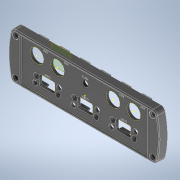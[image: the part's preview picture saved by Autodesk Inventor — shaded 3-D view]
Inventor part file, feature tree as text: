
AUTODESK INVENTOR PART (.ipt)
format: ipt  version: 2021 (Build 250183000, 183)  size: 1,043,968 bytes
history: native  units: mm
features: sketch x8, extrude x7, chamfer x5, plane x3, fillet x2, mirror x1, hole x1, other x1
ambient origin geometry x8: Origin, YZ Plane, XZ Plane, XY Plane, X Axis, Y Axis, Z Axis, Center Point
bodies: Solid1 (feature_tree)
feature tree (28):
  extrude  "Extrusion1"  TaperAngle=0.0deg  [1 undecoded]
  fillet  "Fillet1"  Radius=6.9mm
  plane  "Work Plane1"
  extrude  "Extrusion4"  [1 undecoded]
  chamfer  "Chamfer2"  [1 undecoded]
  mirror  "Mirror1"
  plane  "Work Plane2"
  extrude  "Extrusion7"  Depth=0.2mm TaperAngle=45.0deg
  chamfer  "Chamfer3"  Distance=5.225mm
  hole  "Hole1"  [1 undecoded]
  plane  "Work Plane3"
  extrude  "Extrusion11"  Depth=0.2mm
  extrude  "Extrusion12"  Depth=0.2mm
  fillet  "Fillet4"  Radius=7.0mm
  chamfer  "Chamfer4"  Distance=10.0mm
  chamfer  "Chamfer5"  Distance=0.5mm Angle=45.0deg
  extrude  "Extrusion13"  Depth=0.2mm
  sketch  "Sketch20"  dims[d44=0.0mm]
  extrude  "Extrusion14"  Depth=0.2mm
  chamfer  "Chamfer6"  Distance=12.0mm
  sketch  "Sketch1"  dims[d3=9.0mm d15=0.0mm d16=0.0mm d21=6.9mm]
  sketch  "Sketch5"  dims[d23=1.35mm d26=-1.5mm]
  sketch  "Sketch15"  dims[d40=15.4mm]
  sketch  "Sketch17"  dims[d41=11.5mm]
  sketch  "Sketch18"  dims[d42=54.0mm]
  sketch  "Sketch19"  dims[d43=15.4mm]
  sketch  "Sketch22"  dims[d45=31.0mm d46=0.0mm d47=0.0mm d48=0.2mm d49=2.0mm d50=45.0deg d65=4.85mm d66=4.85mm d67=27.0mm d68=9.0mm d69=3.3mm d70=3.3mm d71=24.0mm d72=16.55mm d73=11.55mm d74=6.35mm d75=1.85mm d76=5.225mm d77=6.9mm d78=10.075mm d79=10.075mm d80=42.584mm d82=7.0mm d83=10.0mm d84=0.0mm d85=0.5mm d86=2.0mm d87=45.0deg d101=10.075mm d102=4.85mm d103=4.85mm d104=27.0mm d105=9.0mm d106=3.3mm d107=3.3mm d108=24.0mm d109=17.55mm d110=11.55mm d111=6.35mm d112=1.85mm d113=4.725mm d114=10.075mm d115=12.0mm d116=6.9mm d117=42.584mm d118=7.0mm d119=7.0mm d122=12.0mm d127=3.25mm d128=6.0mm d129=6.25mm d130=2.0mm d131=90.0deg d132=8.0mm d133=20.594885mm d136=10.0mm d137=0.0mm d138=0.2mm d139=0.0mm d140=3.0mm d141=0.2mm d142=2.0mm d143=45.0deg d144=0.2mm d145=2.0mm d146=45.0deg d147=10.0mm d148=0.0mm d149=8.0mm d150=12.5mm d151=8.0mm d152=12.5mm d153=12.5mm d154=8.0mm d155=8.0mm d156=12.5mm d157=4.5mm d160=4.5mm d161=1.0mm d164=1.0mm d167=28.699852mm d169=20.0mm d171=42.584mm d172=10.0mm d174=10.0mm d176=7.0mm d177=7.0mm d178=7.0mm d179=1.0mm d180=4.5mm d181=4.725mm d185=6.5mm d186=10.0mm d187=0.0mm d188=0.2mm d189=2.0mm d190=45.0deg]
  other  "1009799_3D"
note: 4 required parameter values undecoded (feature->parameter linkage not recoverable at this tier; creation-order binding heuristic only, values carry confidence <= 0.55)
